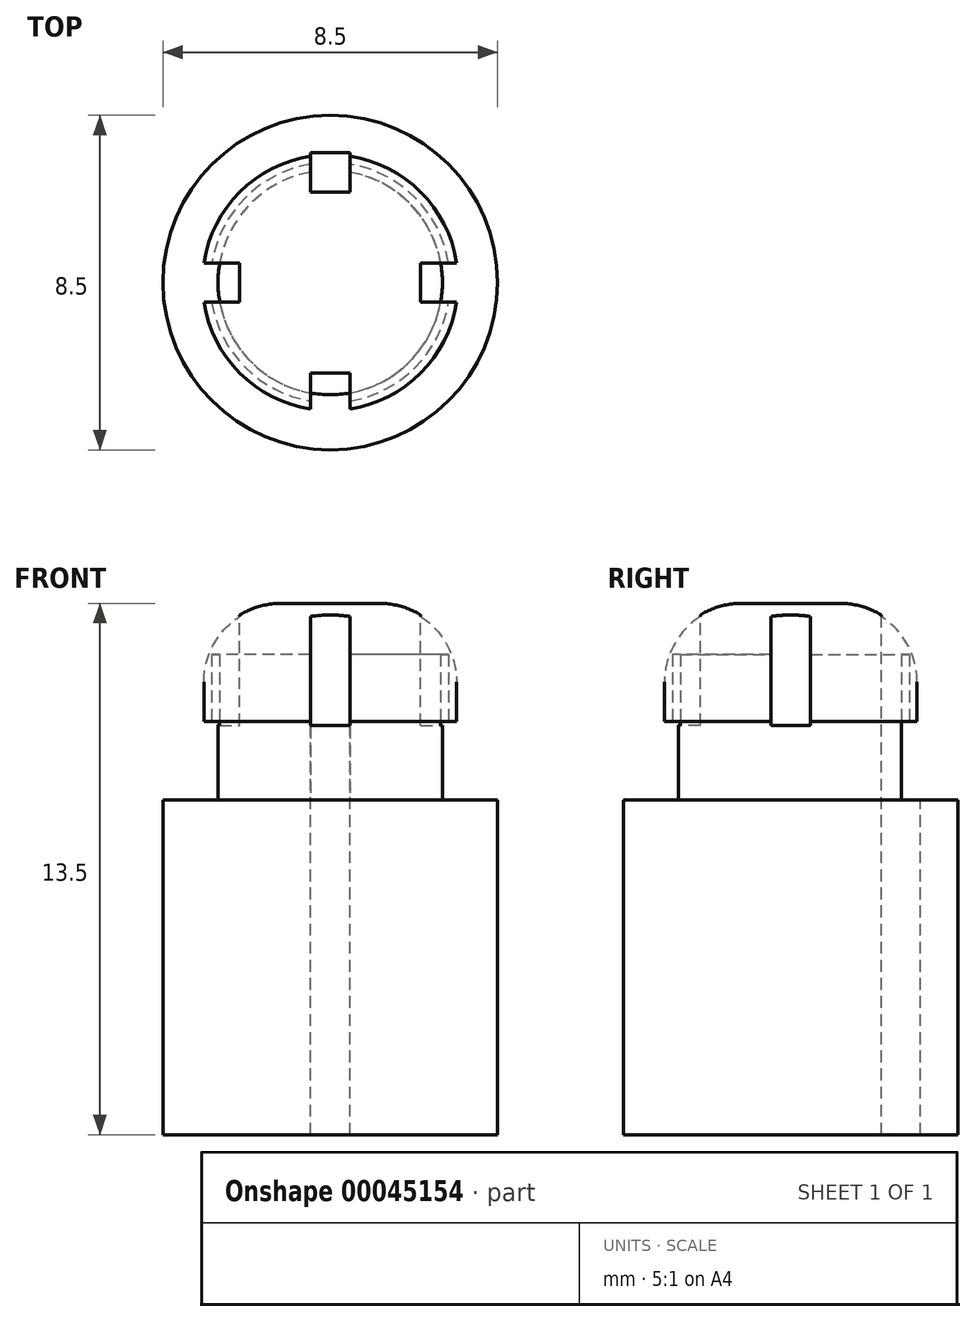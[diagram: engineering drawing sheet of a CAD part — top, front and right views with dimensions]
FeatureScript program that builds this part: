
annotation { "Feature Type Name" : "Feature", "Feature Type Description" : "" }
export const myFeature = defineFeature(function(context is Context, id is Id, definition is map)
    precondition{}
    {
        {
            var Q0;
            Q0=qCreatedBy(makeId("Top.planeOp"),FACE);
            var sketch = newSketch(context, id + "F0", { "sketchPlane" : qUnion([Q0])});
            skCircle(sketch, "E0", {"center": v(0, 0) * mm, "radius": 4.25 * mm});
            skSolve(sketch);
        }
        {
            var Q0;
            Q0 = qSketchRegion(id + "F0", true);
            extrude(context, id + "F1", {"entities" : qUnion([Q0]), "depth" : 8.5 * mm});
        }
        {
            var Q0;
            Q0=makeQuery(id+"F1.opExtrude","CAP_FACE",FACE,{"disambiguationData":[OSD([sQuery(id+"F0.wireOp",EDGE,"E0")])],"isStart":false});
            var sketch = newSketch(context, id + "F2", { "sketchPlane" : qUnion([Q0])});
            skCircle(sketch, "E1", {"center": v(0, 0) * mm, "radius": 2.85 * mm});
            skSolve(sketch);
        }
        {
            var Q0;
            Q0 = qSketchRegion(id + "F2", true);
            extrude(context, id + "F3", {"entities" : qUnion([Q0]), "operationType" : NewBodyOperationType.ADD, "depth" : 2 * mm});
        }
        {
            var Q0;
            Q0=makeQuery(id+"F3.opExtrude","CAP_FACE",FACE,{"disambiguationData":[OSD([sQuery(id+"F2.wireOp",EDGE,"E1")])],"isStart":false});
            var sketch = newSketch(context, id + "F4", { "sketchPlane" : qUnion([Q0])});
            skCircle(sketch, "E2", {"center": v(0, 0) * mm, "radius": 3.25 * mm});
            skSolve(sketch);
        }
        {
            var Q0;
            Q0 = qSketchRegion(id + "F4", true);
            extrude(context, id + "F5", {"entities" : qUnion([Q0]), "operationType" : NewBodyOperationType.ADD, "depth" : 3 * mm});
        }
        {
            var Q0;
            Q0=makeQuery(id+"F4.imprint","IMPRINT",FACE,{"disambiguationData":[TD([[makeQuery(id+"F4.imprint","IMPRINT",EDGE,{"derivedFrom":sQuery(id+"F4.wireOp",EDGE,"E2")}),1.0]])]});
            var sketch = newSketch(context, id + "F6", { "sketchPlane" : qUnion([Q0])});
            skCircle(sketch, "E3", {"center": v(0, 0) * mm, "radius": 2.85 * mm});
            skCircle(sketch, "E4", {"center": v(0, 0) * mm, "radius": 3.05 * mm});
            skSolve(sketch);
        }
        {
            var Q0;
            Q0 = qSketchRegion(id + "F6", true);
            extrude(context, id + "F7", {"entities" : qUnion([Q0]), "operationType" : NewBodyOperationType.REMOVE, "depth" : 1.7 * mm});
        }
        {
            var Q0;
            Q0=makeQuery(id+"F5.opExtrude","CAP_FACE",FACE,{"disambiguationData":[OSD([sQuery(id+"F4.wireOp",EDGE,"E2")])],"isStart":false});
            var sketch = newSketch(context, id + "F8", { "sketchPlane" : qUnion([Q0])});
            skLineSegment(sketch, "E5.bottom", {"start": v(-0.5, -2.3) * mm, "end": v(0.5, -2.3) * mm});
            skLineSegment(sketch, "E5.top", {"start": v(-0.5, -3.3) * mm, "end": v(0.5, -3.3) * mm});
            skLineSegment(sketch, "E5.left", {"start": v(-0.5, -2.3) * mm, "end": v(-0.5, -3.3) * mm});
            skLineSegment(sketch, "E5.right", {"start": v(0.5, -2.3) * mm, "end": v(0.5, -3.3) * mm});
            skSolve(sketch);
        }
        {
            var Q0;
            Q0 = qSketchRegion(id + "F8", true);
            extrude(context, id + "F9", {"entities" : qUnion([Q0]), "operationType" : NewBodyOperationType.REMOVE, "oppositeDirection" : true, "depth" : 3.1 * mm});
        }
        {
            var Q0;
            Q0=makeQuery(id+"F5.opExtrude","CAP_EDGE",EDGE,{"disambiguationData":[OSD([sQuery(id+"F4.wireOp",EDGE,"E2")])],"isStart":false});
            fillet(context, id + "F10", {"entities" : qUnion([Q0]), "radius" : 2 * mm, "tangentPropagation" : true, "allowEdgeOverflow" : false});
        }
        {
            var Q0;
            Q0=makeQuery(id+"F5.opExtrude","CAP_FACE",FACE,{"disambiguationData":[OSD([sQuery(id+"F4.wireOp",EDGE,"E2")])],"isStart":false});
            var sketch = newSketch(context, id + "F11", { "sketchPlane" : qUnion([Q0])});
            skLineSegment(sketch, "E6.bottom", {"start": v(-0.5, 3.3) * mm, "end": v(0.5, 3.3) * mm});
            skLineSegment(sketch, "E6.top", {"start": v(-0.5, 2.3) * mm, "end": v(0.5, 2.3) * mm});
            skLineSegment(sketch, "E6.left", {"start": v(-0.5, 3.3) * mm, "end": v(-0.5, 2.3) * mm});
            skLineSegment(sketch, "E6.right", {"start": v(0.5, 3.3) * mm, "end": v(0.5, 2.3) * mm});
            skSolve(sketch);
        }
        {
            var Q0;
            Q0=makeQuery(id+"F5.opExtrude","CAP_FACE",FACE,{"disambiguationData":[OSD([sQuery(id+"F4.wireOp",EDGE,"E2")])],"isStart":false});
            var sketch = newSketch(context, id + "F12", { "sketchPlane" : qUnion([Q0])});
            skLineSegment(sketch, "E7.bottom", {"start": v(2.3, 0.5) * mm, "end": v(3.3, 0.5) * mm});
            skLineSegment(sketch, "E7.top", {"start": v(2.3, -0.5) * mm, "end": v(3.3, -0.5) * mm});
            skLineSegment(sketch, "E7.left", {"start": v(2.3, 0.5) * mm, "end": v(2.3, -0.5) * mm});
            skLineSegment(sketch, "E7.right", {"start": v(3.3, 0.5) * mm, "end": v(3.3, -0.5) * mm});
            skSolve(sketch);
        }
        {
            var Q0;
            Q0 = qSketchRegion(id + "F12", true);
            extrude(context, id + "F13", {"entities" : qUnion([Q0]), "operationType" : NewBodyOperationType.REMOVE, "oppositeDirection" : true, "depth" : 3.1 * mm});
        }
        {
            var Q0;
            Q0=makeQuery(id+"F5.opExtrude","CAP_FACE",FACE,{"disambiguationData":[OSD([sQuery(id+"F4.wireOp",EDGE,"E2")])],"isStart":false});
            var sketch = newSketch(context, id + "F14", { "sketchPlane" : qUnion([Q0])});
            skLineSegment(sketch, "E8.bottom", {"start": v(-3.3, 0.5) * mm, "end": v(-2.3, 0.5) * mm});
            skLineSegment(sketch, "E8.top", {"start": v(-3.3, -0.5) * mm, "end": v(-2.3, -0.5) * mm});
            skLineSegment(sketch, "E8.left", {"start": v(-3.3, 0.5) * mm, "end": v(-3.3, -0.5) * mm});
            skLineSegment(sketch, "E8.right", {"start": v(-2.3, 0.5) * mm, "end": v(-2.3, -0.5) * mm});
            skSolve(sketch);
        }
        {
            var Q0;
            Q0 = qSketchRegion(id + "F14", true);
            extrude(context, id + "F15", {"entities" : qUnion([Q0]), "operationType" : NewBodyOperationType.REMOVE, "oppositeDirection" : true, "depth" : 3.1 * mm});
        }
        {
            var Q0;
            Q0 = qSketchRegion(id + "F11", true);
            extrude(context, id + "F16", {"entities" : qUnion([Q0]), "operationType" : NewBodyOperationType.REMOVE, "oppositeDirection" : true, "depth" : 78.74 * mm});
        }
    });
